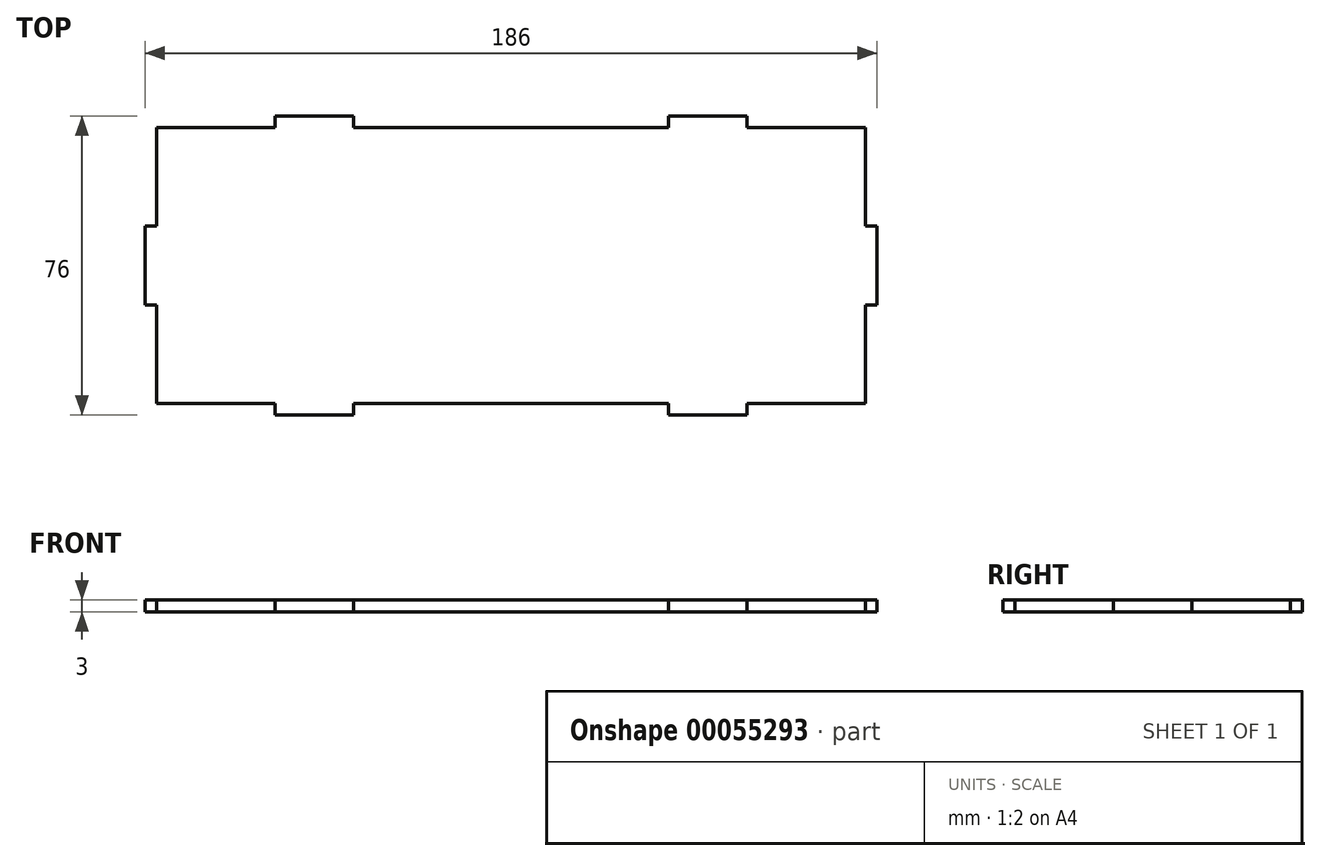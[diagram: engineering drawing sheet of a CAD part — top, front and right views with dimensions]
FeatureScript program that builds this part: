
annotation { "Feature Type Name" : "Feature", "Feature Type Description" : "" }
export const myFeature = defineFeature(function(context is Context, id is Id, definition is map)
    precondition{}
    {
        {
            assignVariable(context, id + "F0", {"name" : "PanelThickness", "anyValue" : 3});
        }
        {
            var Q0;
            Q0=qCreatedBy(makeId("Top.planeOp"),FACE);
            var sketch = newSketch(context, id + "F1", { "sketchPlane" : qUnion([Q0])});
            skLineSegment(sketch, "E0.rect.bottom", {"start": v(90, 35) * mm, "end": v(60, 35) * mm});
            skLineSegment(sketch, "E0.rect.top", {"start": v(90, -35) * mm, "end": v(60, -35) * mm});
            skLineSegment(sketch, "E0.rect.left", {"start": v(90, 35) * mm, "end": v(90, 10) * mm});
            skLineSegment(sketch, "E0.rect.right", {"start": v(-90, 35) * mm, "end": v(-90, 10) * mm});
            skLineSegment(sketch, "E1.top", {"start": v(40, -38) * mm, "end": v(60, -38) * mm});
            skLineSegment(sketch, "E1.left", {"start": v(40, -35) * mm, "end": v(40, -38) * mm});
            skLineSegment(sketch, "E1.right", {"start": v(60, -35) * mm, "end": v(60, -38) * mm});
            skLineSegment(sketch, "E2.MirrorCS", {"start": v(-40, -35) * mm, "end": v(-40, -38) * mm});
            skLineSegment(sketch, "E3.MirrorCS", {"start": v(-40, -38) * mm, "end": v(-60, -38) * mm});
            skLineSegment(sketch, "E4.MirrorCS", {"start": v(-60, -35) * mm, "end": v(-60, -38) * mm});
            skLineSegment(sketch, "E5.MirrorCS", {"start": v(-40, 38) * mm, "end": v(-60, 38) * mm});
            skLineSegment(sketch, "E6.MirrorCS", {"start": v(-40, 35) * mm, "end": v(-40, 38) * mm});
            skLineSegment(sketch, "E7.MirrorCS", {"start": v(-60, 35) * mm, "end": v(-60, 38) * mm});
            skLineSegment(sketch, "E8.MirrorCS", {"start": v(40, 35) * mm, "end": v(40, 38) * mm});
            skLineSegment(sketch, "E9.MirrorCS", {"start": v(40, 38) * mm, "end": v(60, 38) * mm});
            skLineSegment(sketch, "E10.MirrorCS", {"start": v(60, 35) * mm, "end": v(60, 38) * mm});
            skLineSegment(sketch, "E11.bottom", {"start": v(-90, -10) * mm, "end": v(-93, -10) * mm});
            skLineSegment(sketch, "E11.top", {"start": v(-90, 10) * mm, "end": v(-93, 10) * mm});
            skLineSegment(sketch, "E11.right", {"start": v(-93, -10) * mm, "end": v(-93, 10) * mm});
            skPoint(sketch, "E12", {"position": v(-93, 0) * mm});
            skLineSegment(sketch, "E13.MirrorCS", {"start": v(90, -10) * mm, "end": v(93, -10) * mm});
            skLineSegment(sketch, "E14.MirrorCS", {"start": v(93, -10) * mm, "end": v(93, 10) * mm});
            skLineSegment(sketch, "E15.MirrorCS", {"start": v(90, 10) * mm, "end": v(93, 10) * mm});
            skLineSegment(sketch, "E16.0", {"start": v(93, 38) * mm, "end": v(-93, 38) * mm, "construction": true});
            skLineSegment(sketch, "E17.0", {"start": v(-93, 38) * mm, "end": v(-93, -38) * mm, "construction": true});
            skLineSegment(sketch, "E18.0", {"start": v(93, 38) * mm, "end": v(93, -38) * mm, "construction": true});
            skLineSegment(sketch, "E19.0", {"start": v(93, -38) * mm, "end": v(-93, -38) * mm, "construction": true});
            skLineSegment(sketch, "E20", {"start": v(-60, 35) * mm, "end": v(-90, 35) * mm});
            skLineSegment(sketch, "E21", {"start": v(40, 35) * mm, "end": v(-40, 35) * mm});
            skLineSegment(sketch, "E22", {"start": v(90, -10) * mm, "end": v(90, -35) * mm});
            skLineSegment(sketch, "E23", {"start": v(40, -35) * mm, "end": v(-40, -35) * mm});
            skLineSegment(sketch, "E24", {"start": v(-60, -35) * mm, "end": v(-90, -35) * mm});
            skLineSegment(sketch, "E25", {"start": v(-90, -10) * mm, "end": v(-90, -35) * mm});
            skLineSegment(sketch, "E26", {"start": v(-200, 44.97) * mm, "end": v(-200, -58.1) * mm});
            skSolve(sketch);
        }
        {
            var Q0;
            {var subQ1=sQuery(id+"F1.wireOp",EDGE,"E1.bottom");Q0=makeQuery(id+"F1.imprint","IMPRINT",FACE,{"disambiguationData":[TD([[makeQuery(id+"F1.imprint","IMPRINT",EDGE,{"derivedFrom":subQ1}),1.0]])]});}
            var Q1;
            Q1=makeQuery(id+"F1.imprint","IMPRINT",FACE,{"disambiguationData":[TD([[makeQuery(id+"F1.imprint","IMPRINT",EDGE,{"derivedFrom":sQuery(id+"F1.wireOp",EDGE,"E11.bottom")}),-1.0]])]});
            var Q2;
            Q2=makeQuery(id+"F1.imprint","IMPRINT",FACE,{"disambiguationData":[TD([[makeQuery(id+"F1.imprint","IMPRINT",EDGE,{"derivedFrom":sQuery(id+"F1.wireOp",EDGE,"E5.MirrorCS")}),1.0]])]});
            var Q3;
            {var subQ1=sQuery(id+"F1.wireOp",EDGE,"E8.MirrorCS");Q3=makeQuery(id+"F1.imprint","IMPRINT",FACE,{"disambiguationData":[TD([[makeQuery(id+"F1.imprint","IMPRINT",EDGE,{"derivedFrom":subQ1}),-1.0]])]});}
            var Q4;
            {var subQ1=sQuery(id+"F1.wireOp",EDGE,"E13.MirrorCS");Q4=makeQuery(id+"F1.imprint","IMPRINT",FACE,{"disambiguationData":[TD([[makeQuery(id+"F1.imprint","IMPRINT",EDGE,{"derivedFrom":subQ1}),1.0]])]});}
            var Q5;
            Q5=makeQuery(id+"F1.imprint","IMPRINT",FACE,{"disambiguationData":[TD([[makeQuery(id+"F1.imprint","IMPRINT",EDGE,{"derivedFrom":sQuery(id+"F1.wireOp",EDGE,"E1.bottom")}),-1.0]])]});
            var Q6;
            {var subQ1=sQuery(id+"F1.wireOp",EDGE,"E2.MirrorCS");Q6=makeQuery(id+"F1.imprint","IMPRINT",FACE,{"disambiguationData":[TD([[makeQuery(id+"F1.imprint","IMPRINT",EDGE,{"derivedFrom":subQ1}),-1.0]])]});}
            extrude(context, id + "F2", {"entities" : qUnion([Q0, Q1, Q2, Q3, Q4, Q5, Q6]), "depth" : (getVariable(context, 'PanelThickness')) * mm});
        }
    });
